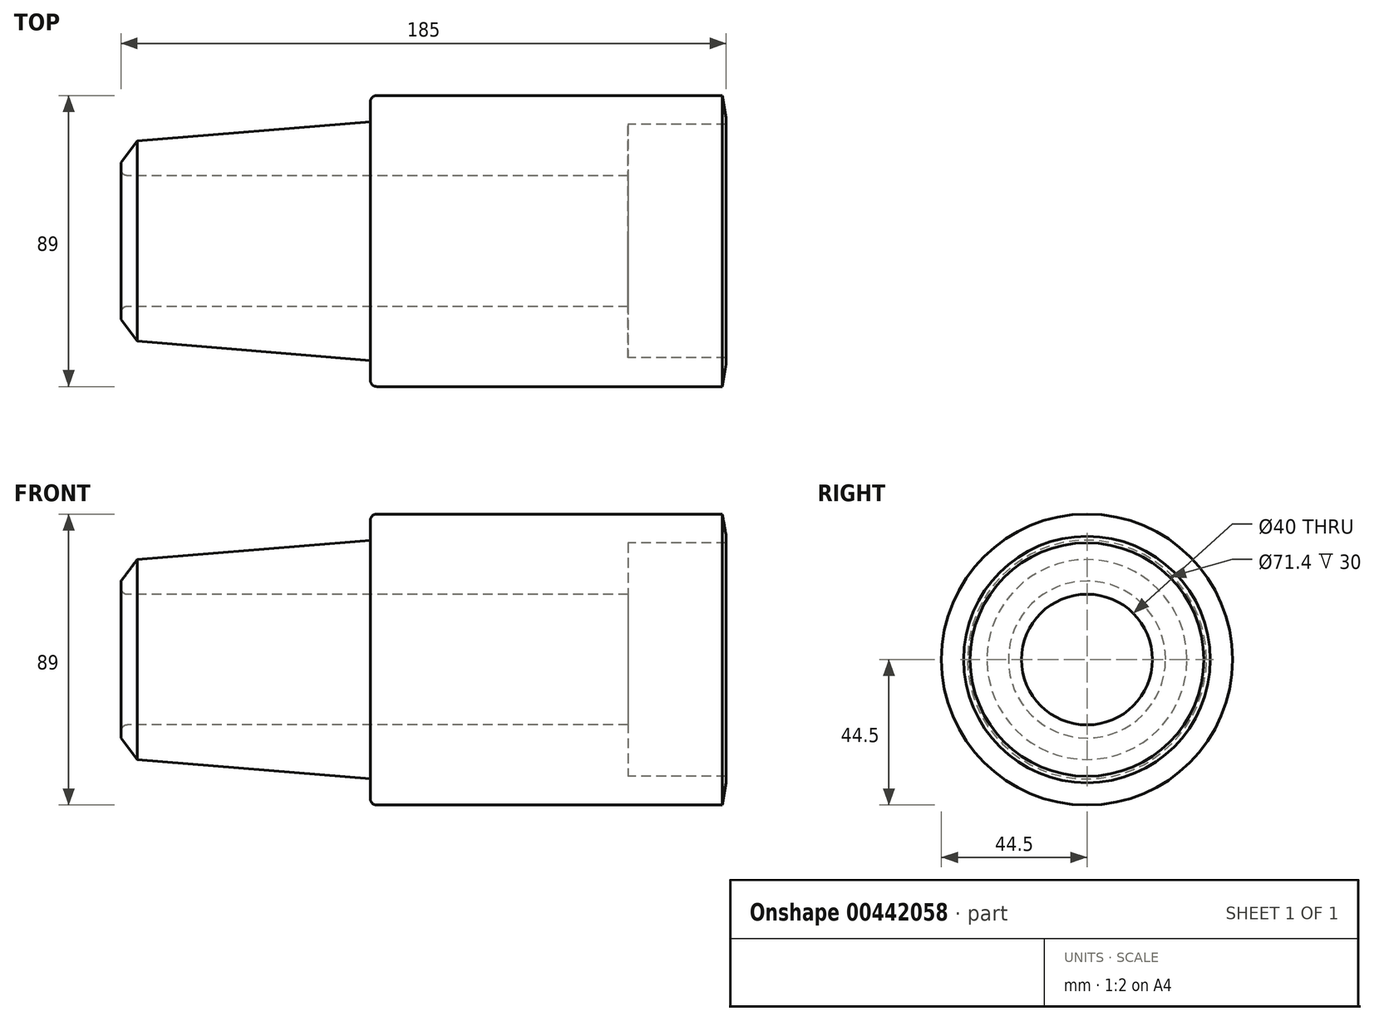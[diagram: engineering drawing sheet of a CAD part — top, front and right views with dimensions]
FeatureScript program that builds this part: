
annotation { "Feature Type Name" : "Feature", "Feature Type Description" : "" }
export const myFeature = defineFeature(function(context is Context, id is Id, definition is map)
    precondition{}
    {
        {
            var Q0;
            Q0=qCreatedBy(makeId("Front.planeOp"),FACE);
            var sketch = newSketch(context, id + "F0", { "sketchPlane" : qUnion([Q0])});
            skLineSegment(sketch, "E0", {"start": v(0, 20) * mm, "end": v(-153, 20) * mm});
            skLineSegment(sketch, "E1", {"start": v(-155, 22) * mm, "end": v(-155, 30.16) * mm, "construction": true});
            skLineSegment(sketch, "E2", {"start": v(-155, 30.16) * mm, "end": v(-78.8, 36.5) * mm, "construction": true});
            skLineSegment(sketch, "E3", {"start": v(-78.8, 36.5) * mm, "end": v(-78.8, 42.5) * mm});
            skLineSegment(sketch, "E4", {"start": v(-76.8, 44.5) * mm, "end": v(28.8, 44.5) * mm});
            skLineSegment(sketch, "E5", {"start": v(28.8, 44.5) * mm, "end": v(30, 37.7) * mm});
            skLineSegment(sketch, "E6", {"start": v(30, 37.7) * mm, "end": v(30, 35.7) * mm});
            skLineSegment(sketch, "E7", {"start": v(30, 35.7) * mm, "end": v(0, 35.7) * mm});
            skLineSegment(sketch, "E8", {"start": v(0, 35.7) * mm, "end": v(0, 20) * mm});
            skLineSegment(sketch, "E9", {"start": v(-218.76, 0) * mm, "end": v(71.92, 0) * mm, "construction": true});
            skLineSegment(sketch, "E10", {"start": v(-155, 24) * mm, "end": v(-150, 30.58) * mm});
            skLineSegment(sketch, "E11", {"start": v(-150, 30.58) * mm, "end": v(-78.8, 36.5) * mm});
            skLineSegment(sketch, "E12", {"start": v(-155, 25.08) * mm, "end": v(-155, 20) * mm});
            skPoint(sketch, "E13.visualSharp", {"position": v(-155, 20) * mm});
            skArc(sketch, "E13.filletArc", {"start": v(-155, 22) * mm, "mid": v(-154.41, 20.59) * mm, "end": v(-153, 20) * mm});
            skPoint(sketch, "E14.visualSharp", {"position": v(-78.8, 44.5) * mm});
            skArc(sketch, "E14.filletArc", {"start": v(-76.8, 44.5) * mm, "mid": v(-78.21, 43.91) * mm, "end": v(-78.8, 42.5) * mm});
            skLineSegment(sketch, "E15", {"start": v(-78.8, 33.69) * mm, "end": v(-175, 25.68) * mm, "construction": true});
            skPoint(sketch, "E16", {"position": v(-155, 27.34) * mm});
            skLineSegment(sketch, "E17", {"start": v(-155, 30.16) * mm, "end": v(-175, 28.5) * mm});
            skLineSegment(sketch, "E18", {"start": v(-86, 25.22) * mm, "end": v(-86, 45.47) * mm, "construction": true});
            skPoint(sketch, "E19", {"position": v(-86, 33.09) * mm});
            skLineSegment(sketch, "E20", {"start": v(-86, 33.09) * mm, "end": v(-82.87, 36.21) * mm});
            skSolve(sketch);
        }
        {
            var Q0;
            Q0=makeQuery(id+"F0.imprint","IMPRINT",FACE,{"disambiguationData":[TD([[makeQuery(id+"F0.imprint","IMPRINT",EDGE,{"derivedFrom":sQuery(id+"F0.wireOp",EDGE,"E0")}),-1.0]])]});
            var Q1;
            Q1=sQuery(id+"F0.wireOp",EDGE,"E9");
            revolve(context, id + "F1", {"entities" : qUnion([Q0]), "axis" : qUnion([Q1]), "revolveType" : RevolveType.FULL});
        }
    });
